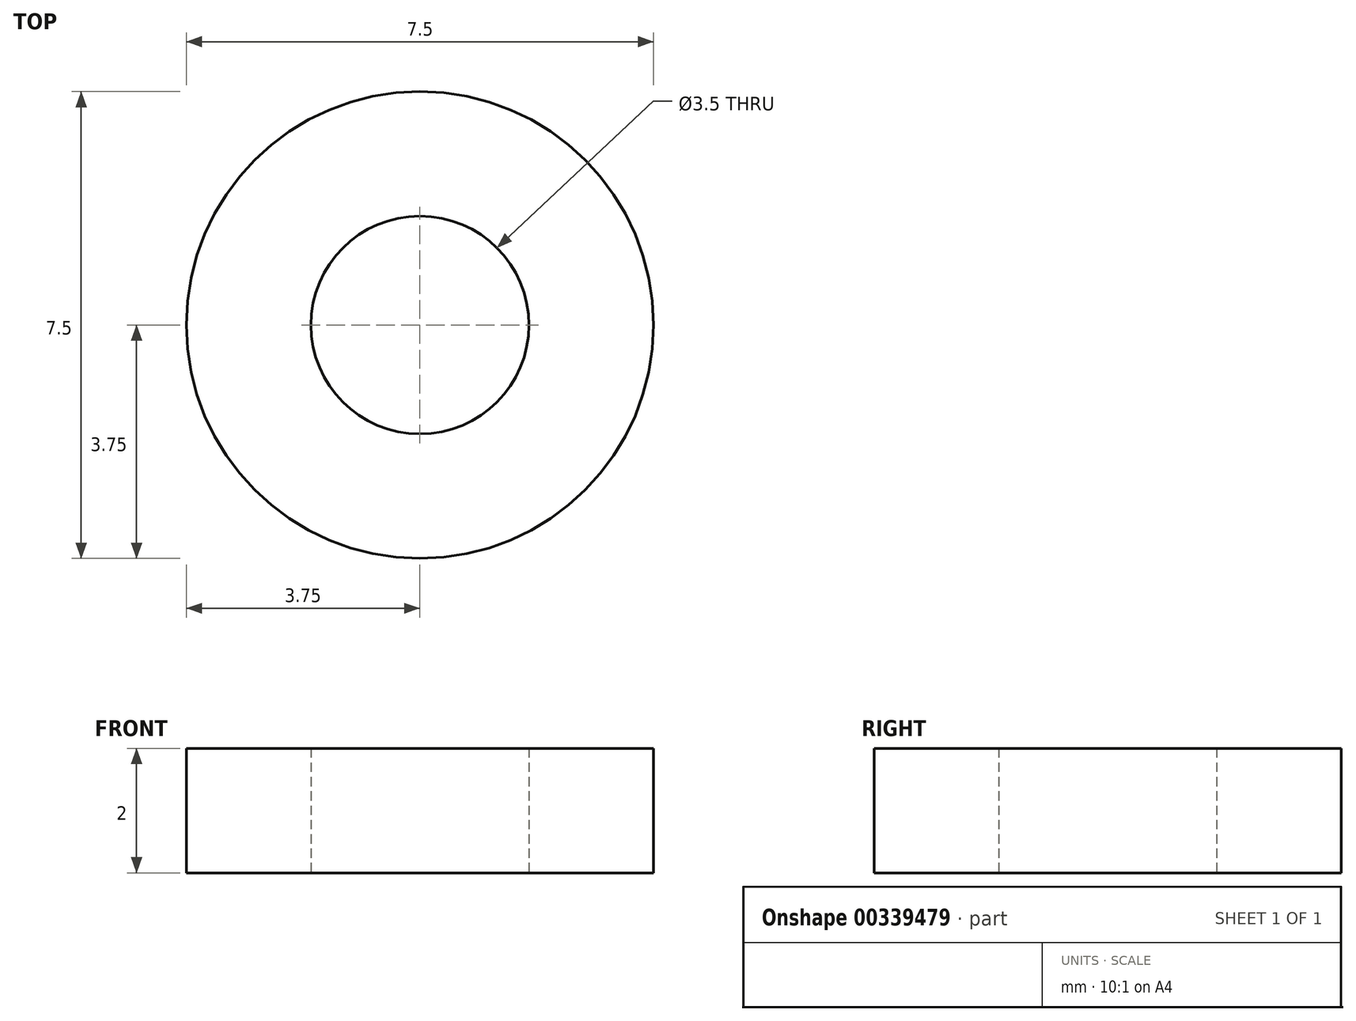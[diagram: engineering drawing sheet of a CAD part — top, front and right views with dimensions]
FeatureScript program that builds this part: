
annotation { "Feature Type Name" : "Feature", "Feature Type Description" : "" }
export const myFeature = defineFeature(function(context is Context, id is Id, definition is map)
    precondition{}
    {
        {
            var Q0;
            Q0=qCreatedBy(makeId("Top.planeOp"),FACE);
            var sketch = newSketch(context, id + "F0", { "sketchPlane" : qUnion([Q0])});
            skCircle(sketch, "E0", {"center": v(0, 0) * mm, "radius": 1.75 * mm});
            skCircle(sketch, "E1", {"center": v(0, 0) * mm, "radius": 3.75 * mm});
            skSolve(sketch);
        }
        {
            var Q0;
            Q0 = qSketchRegion(id + "F0", true);
            extrude(context, id + "F1", {"entities" : qUnion([Q0]), "depth" : 2 * mm});
        }
    });
